AUTODESK INVENTOR PART (.ipt)
format: ipt  version: 2021 (Build 250183000, 183)  size: 37,366,784 bytes
history: native  units: mm
features: other x7, extrude x2, sketch x1
ambient origin geometry x8: Origin, YZ Plane, XZ Plane, XY Plane, X Axis, Y Axis, Z Axis, Center Point
bodies: Body1 (feature_tree)
feature tree (10):
  other  "original"
  other  "dim_aligned"
  other  "shortened"
  other  "base_plate"
  extrude  "plate"  Depth=3.1mm
  extrude  "motor_recess"  Depth=3.1mm
  other  "motor_recess_outline"
  other  "Image1"
  other  "base_plate_fillets"
  sketch  "Sketch8"  dims[d65=2.0mm d84=3.1mm d90=3.1mm d97=2.0mm d99=3.1mm d105=3.1mm d111=3.1mm d117=3.1mm d124=3.1mm d125=3.1mm d126=3.1mm d127=3.1mm d128=3.1mm d129=3.1mm d130=3.1mm d131=3.1mm d132=3.1mm d133=3.1mm d134=3.1mm d135=3.1mm d136=3.1mm d137=3.1mm d138=3.1mm d139=3.1mm d197=2.0mm d201=2.0mm d208=2.0mm d209=2.0mm d214=1.6mm d219=1.6mm d220=5.060505mm d221=10.114204mm d222=24.997185mm d223=8.10111mm d238=2.0mm d239=18.118125mm d240=37.072895mm d241=3.1mm d242=3.1mm d243=3.1mm d250=3.1mm d251=3.1mm d252=3.1mm d253=3.1mm d254=3.1mm d255=3.1mm d256=3.1mm d257=3.1mm d258=3.1mm d259=3.1mm d260=3.1mm d261=3.1mm d262=3.1mm d263=3.1mm d264=3.1mm d265=3.1mm d266=3.1mm d267=3.1mm d268=3.1mm d269=3.1mm d270=3.1mm d271=3.1mm d272=3.1mm d273=3.1mm d274=3.1mm d275=3.1mm d276=3.1mm d277=3.1mm d278=3.1mm d279=3.1mm d280=3.1mm d281=3.1mm d282=3.1mm d283=3.1mm d284=3.1mm d285=3.1mm d353=2.0mm d368=57.663236mm d369=16.042638mm d370=8.0mm d371=15.725mm d372=15.725mm d373=5.2mm d374=5.2mm d375=0.0mm d376=15.0mm d377=15.0mm d378=6.0mm d379=6.0mm d380=12.0mm d381=12.0mm d382=23.0mm d383=23.0mm d384=12.0mm d385=38.9mm d386=38.9mm d387=12.0mm d388=15.0mm d389=15.0mm d390=46.0mm d391=46.0mm d392=46.0mm d393=30.0mm d394=30.0mm d395=46.0mm d396=29.0mm d397=29.0mm d400=12.0mm d401=12.0mm d403=84.0mm d404=84.0mm d405=74.0mm d406=74.0mm d407=24.0mm d408=38.0mm d409=86.0mm d410=86.0mm d411=93.0mm d412=0.0mm d413=15.0mm d414=15.0mm d415=0.4mm d416=0.4mm d417=6.6mm d418=6.6mm d419=12.0mm d420=12.0mm d421=12.0mm d422=12.0mm d423=22.6mm d424=22.6mm d425=42.6mm d426=42.6mm d427=14.0mm d428=14.0mm d429=29.0mm d430=29.0mm d431=42.6mm d432=42.6mm d433=56.6mm d434=56.6mm d435=12.0mm d436=12.0mm d437=72.7mm d438=72.7mm d439=24.0mm d440=38.0mm d441=12.0mm d442=73.5mm d443=73.5mm d444=12.0mm d445=106.0mm d446=113.0mm d447=120.0mm d448=146.0mm d449=154.0mm d450=110.6mm d525=15.0mm d526=15.0mm d527=0.4mm d528=0.4mm d529=6.6mm d530=6.6mm d531=12.0mm d532=12.0mm d533=12.0mm d534=12.0mm d535=22.6mm d536=22.6mm d537=42.6mm d538=42.6mm d539=14.0mm d540=14.0mm d541=29.0mm d542=29.0mm d543=42.6mm d544=42.6mm d545=56.6mm d546=56.6mm d547=12.0mm d548=12.0mm d549=72.7mm d550=72.7mm d551=24.0mm d552=38.0mm d553=12.0mm d554=73.5mm d555=73.5mm d556=12.0mm d557=110.6mm d558=246.6mm d576=3.1mm d577=2.0mm d579=4.0mm d582=16.0mm d583=6.0mm d584=6.0mm d585=8.0mm d587=18.2mm d589=2.9mm d594=9.4mm d595=16.0mm d596=58.0mm d597=46.0mm d598=5.1mm d599=68.0mm d600=40.0mm d601=6.0mm d603=40.0mm d604=94.0mm d605=80.0mm d606=60.0mm d607=4.0mm d608=8.6mm d611=19.1mm d612=4.0mm d614=20.0mm d615=0.0mm d616=41.54mm d617=1.745329mm d620=12.0mm d622=3.0mm d627=10.0mm d629=6.2mm d631=6.2mm d632=6.2mm d633=6.2mm d634=6.2mm d635=6.2mm d636=6.2mm d637=6.2mm d638=6.2mm d639=5.0mm d640=5.0mm d641=6.2mm d642=6.2mm d643=6.2mm d644=6.2mm d645=6.2mm d646=6.2mm d647=6.2mm d648=2.0mm d649=3.1mm d650=3.1mm d652=3.1mm d653=3.1mm d654=3.1mm d658=3.1mm d659=49.0mm d660=67.1mm d661=37.0mm d671=46.0mm d677=30.970563mm d678=20.0mm d680=16.970563mm d681=20.0mm d683=16.970563mm d686=8.0mm d687=16.970563mm d688=3.1mm d689=6.0mm d690=8.0mm d691=8.485281mm d692=3.1mm d693=16.0mm d694=8.0mm d695=45.1mm d696=12.0mm d697=6.2mm d698=6.2mm d702=3.1mm d706=14.0mm d707=14.0mm d708=14.0mm d709=14.0mm d712=110.0mm d714=16.0mm d722=3.0mm d723=0.0mm d724=0.6mm d725=0.0mm d742=8.0mm d744=0.0001mm d745=4.1mm d746=0.0001mm d747=4.1mm d748=0.0001mm d749=4.1mm d750=0.0001mm d751=4.1mm d755=32.0mm d756=16.0mm d758=14.0mm d623=0.872665mm d624=0.5mm d625=0.872665mm d626=0.872665mm d655=0.5mm d656=0.872665mm d699=0.5mm d700=0.872665mm d701=0.5mm d715=0.5mm d716=0.872665mm d717=0.5mm d718=0.872665mm]
